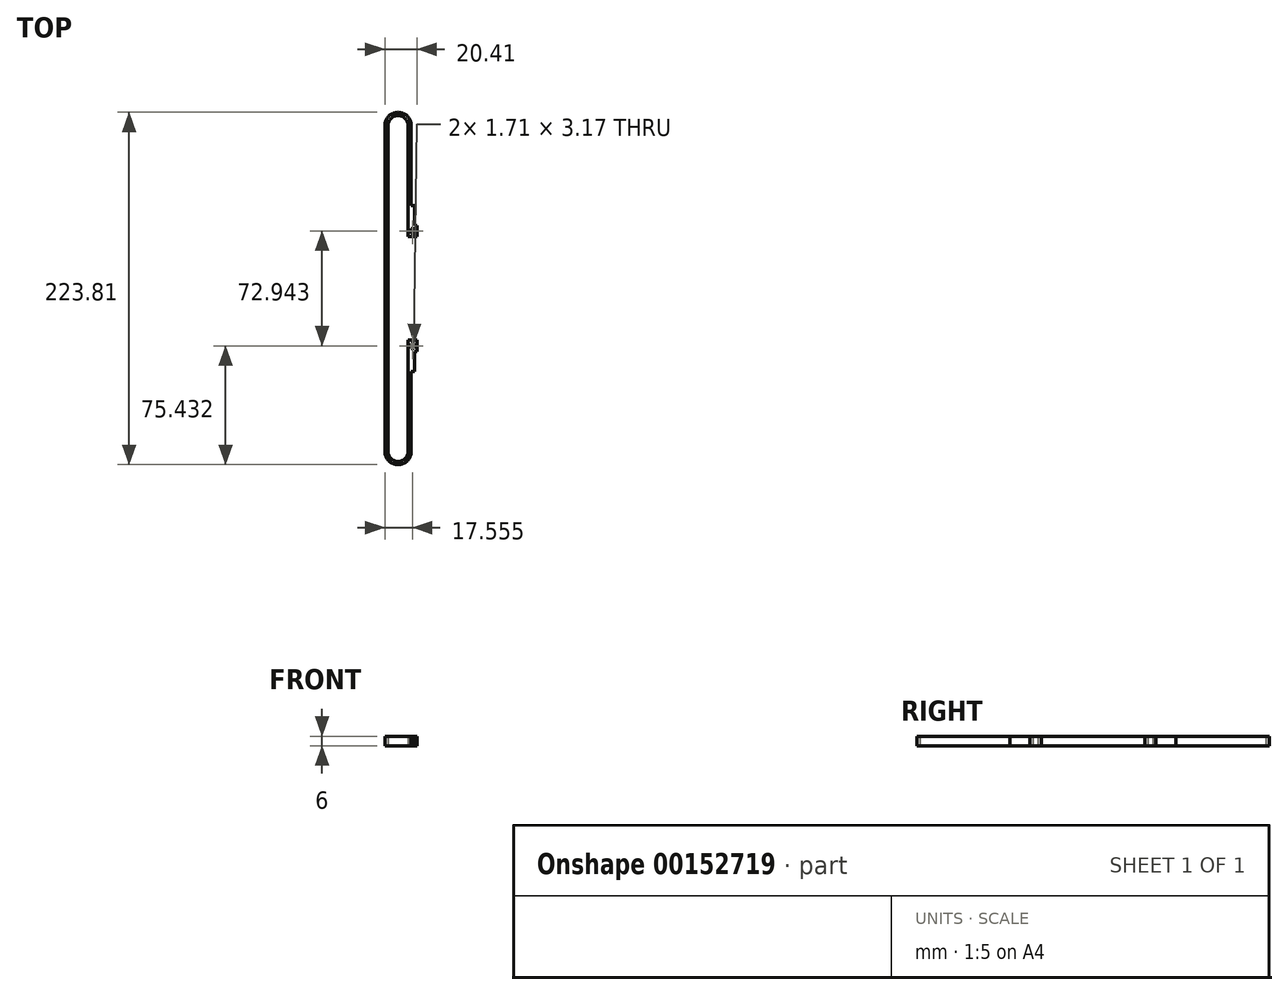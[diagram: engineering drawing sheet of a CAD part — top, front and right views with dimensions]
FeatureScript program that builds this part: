
annotation { "Feature Type Name" : "Feature", "Feature Type Description" : "" }
export const myFeature = defineFeature(function(context is Context, id is Id, definition is map)
    precondition{}
    {
        {
            var Q0;
            Q0=qCreatedBy(makeId("Top.planeOp"),FACE);
            var sketch = newSketch(context, id + "F0", { "sketchPlane" : qUnion([Q0])});
            skLineSegment(sketch, "E0.bottom", {"start": v(0, 0) * mm, "end": v(1.7, 0) * mm});
            skLineSegment(sketch, "E0.top", {"start": v(0, -3.18) * mm, "end": v(1.7, -3.18) * mm});
            skLineSegment(sketch, "E0.left", {"start": v(0, 0) * mm, "end": v(0, -3.18) * mm});
            skLineSegment(sketch, "E0.right", {"start": v(1.7, 0) * mm, "end": v(1.7, -3.18) * mm});
            skLineSegment(sketch, "E1", {"start": v(0, -1.59) * mm, "end": v(-2, -1.59) * mm, "construction": true});
            skLineSegment(sketch, "E2", {"start": v(1.7, -1.59) * mm, "end": v(3.7, -1.59) * mm, "construction": true});
            skLineSegment(sketch, "E3", {"start": v(0.85, 0) * mm, "end": v(0.85, 2) * mm, "construction": true});
            skLineSegment(sketch, "E4", {"start": v(0.85, -3.18) * mm, "end": v(0.85, -5.18) * mm, "construction": true});
            skLineSegment(sketch, "E5.top", {"start": v(-2, 2) * mm, "end": v(3.7, 2) * mm});
            skLineSegment(sketch, "E5.left", {"start": v(-2, -68.68) * mm, "end": v(-2, 2) * mm});
            skLineSegment(sketch, "E5.right", {"start": v(3.7, -5.18) * mm, "end": v(3.7, 2) * mm});
            skLineSegment(sketch, "E6", {"start": v(-2, -68.68) * mm, "end": v(0, -68.68) * mm, "construction": true});
            skLineSegment(sketch, "E7", {"start": v(-2, -68.68) * mm, "end": v(-14.7, -68.68) * mm, "construction": true});
            skLineSegment(sketch, "E8", {"start": v(-14.7, -68.67) * mm, "end": v(-16.7, -68.67) * mm, "construction": true});
            skArc(sketch, "E9", {"start": v(-14.7, -68.68) * mm, "mid": v(-8.35, -75.03) * mm, "end": v(-2, -68.68) * mm});
            skArc(sketch, "E10", {"start": v(-16.7, -68.67) * mm, "mid": v(-8.35, -77.03) * mm, "end": v(0, -68.68) * mm});
            skLineSegment(sketch, "E11", {"start": v(0, -68.68) * mm, "end": v(0, -17.88) * mm});
            skLineSegment(sketch, "E12", {"start": v(3.7, -5.18) * mm, "end": v(2, -5.18) * mm});
            skLineSegment(sketch, "E13", {"start": v(2, -5.18) * mm, "end": v(2, -17.88) * mm});
            skLineSegment(sketch, "E14", {"start": v(2, -17.88) * mm, "end": v(0, -17.88) * mm});
            skLineSegment(sketch, "E15", {"start": v(0.85, -5.18) * mm, "end": v(2, -5.18) * mm});
            skLineSegment(sketch, "E16", {"start": v(0.85, 2) * mm, "end": v(0.85, 67.77) * mm, "construction": true});
            skLineSegment(sketch, "E17", {"start": v(0.85, 67.77) * mm, "end": v(0.85, 69.77) * mm, "construction": true});
            skLineSegment(sketch, "E18.bottom", {"start": v(1.7, 72.94) * mm, "end": v(0, 72.94) * mm});
            skLineSegment(sketch, "E18.top", {"start": v(1.7, 69.77) * mm, "end": v(0, 69.77) * mm});
            skLineSegment(sketch, "E18.left", {"start": v(1.7, 72.94) * mm, "end": v(1.7, 69.77) * mm});
            skLineSegment(sketch, "E18.right", {"start": v(0, 72.94) * mm, "end": v(0, 69.77) * mm});
            skLineSegment(sketch, "E19", {"start": v(0, 71.36) * mm, "end": v(-2, 71.36) * mm, "construction": true});
            skLineSegment(sketch, "E20", {"start": v(1.7, 71.36) * mm, "end": v(3.7, 71.36) * mm, "construction": true});
            skLineSegment(sketch, "E21", {"start": v(0.85, 72.94) * mm, "end": v(0.85, 74.94) * mm, "construction": true});
            skLineSegment(sketch, "E22", {"start": v(3.7, 67.77) * mm, "end": v(-2, 67.77) * mm});
            skLineSegment(sketch, "E23", {"start": v(-2, 67.77) * mm, "end": v(-2, 138.44) * mm});
            skLineSegment(sketch, "E24", {"start": v(3.7, 67.77) * mm, "end": v(3.7, 74.94) * mm});
            skLineSegment(sketch, "E25", {"start": v(3.7, 74.94) * mm, "end": v(2, 74.94) * mm});
            skLineSegment(sketch, "E26", {"start": v(2, 74.94) * mm, "end": v(2, 87.64) * mm});
            skLineSegment(sketch, "E27", {"start": v(2, 87.64) * mm, "end": v(0, 87.64) * mm});
            skLineSegment(sketch, "E28", {"start": v(0, 87.64) * mm, "end": v(0, 138.44) * mm});
            skLineSegment(sketch, "E29", {"start": v(-2, 138.44) * mm, "end": v(0, 138.44) * mm, "construction": true});
            skLineSegment(sketch, "E30", {"start": v(-2, 138.44) * mm, "end": v(-14.7, 138.44) * mm, "construction": true});
            skLineSegment(sketch, "E31", {"start": v(-14.7, 138.44) * mm, "end": v(-16.7, 138.44) * mm, "construction": true});
            skArc(sketch, "E32", {"start": v(-2, 138.44) * mm, "mid": v(-8.35, 144.8) * mm, "end": v(-14.7, 138.44) * mm});
            skArc(sketch, "E33", {"start": v(0, 138.44) * mm, "mid": v(-8.35, 146.8) * mm, "end": v(-16.7, 138.44) * mm});
            skLineSegment(sketch, "E34", {"start": v(-14.7, -68.68) * mm, "end": v(-14.7, 138.44) * mm});
            skLineSegment(sketch, "E35", {"start": v(-16.7, 138.44) * mm, "end": v(-16.7, -68.67) * mm});
            skLineSegment(sketch, "E36", {"start": v(0.85, 74.94) * mm, "end": v(2, 74.94) * mm, "construction": true});
            skSolve(sketch);
        }
        {
            var Q0;
            Q0 = qSketchRegion(id + "F0", true);
            extrude(context, id + "F1", {"entities" : qUnion([Q0]), "depth" : 6 * mm});
        }
    });
